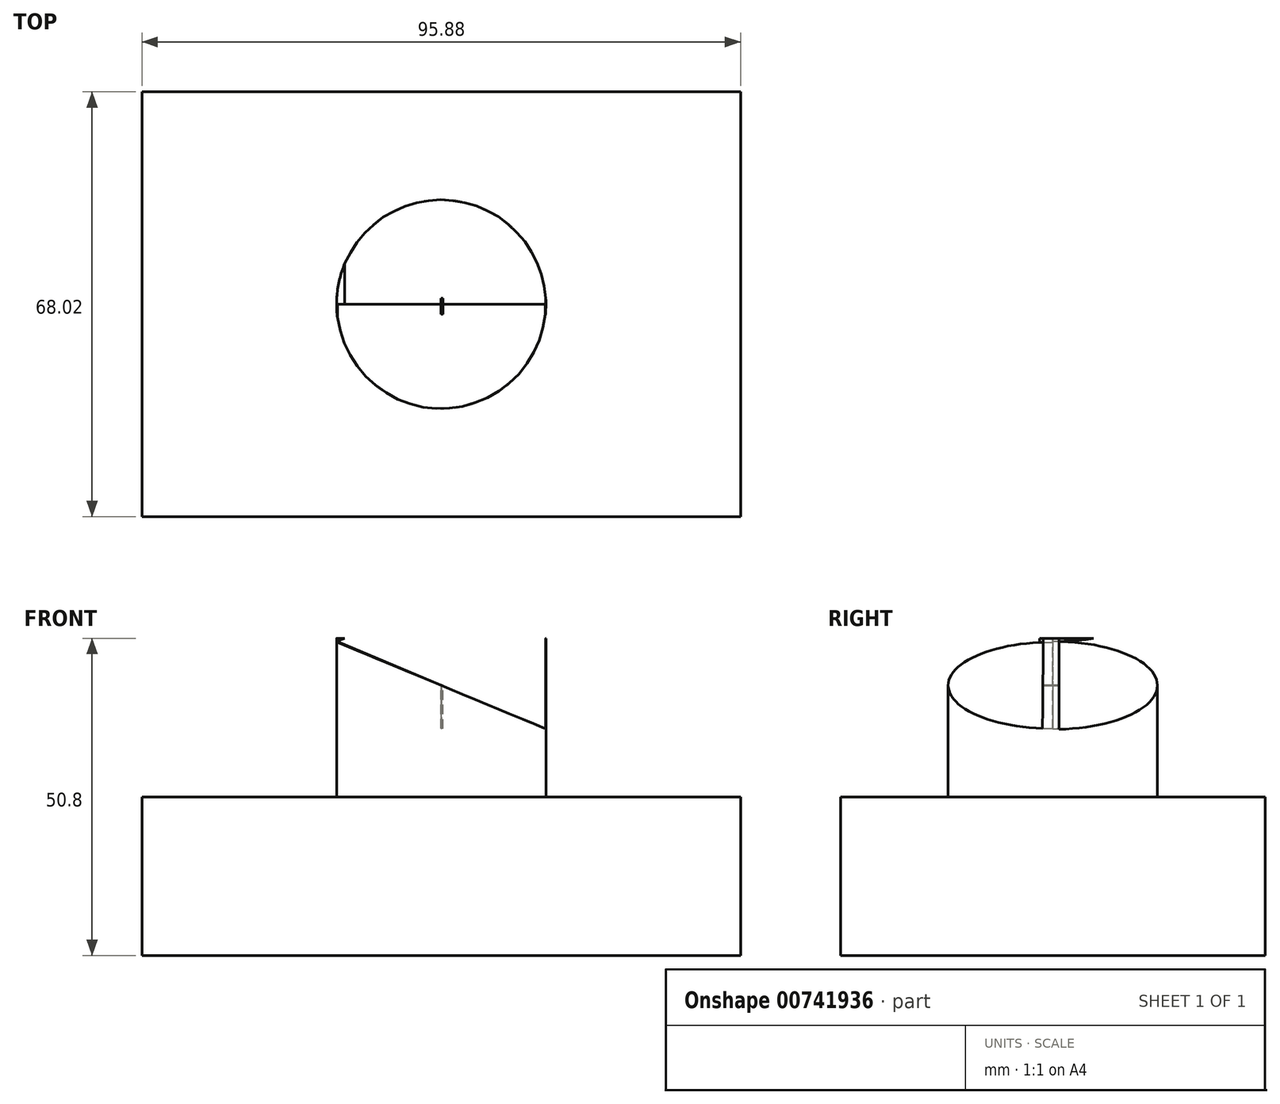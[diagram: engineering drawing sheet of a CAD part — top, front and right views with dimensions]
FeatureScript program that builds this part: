
annotation { "Feature Type Name" : "Feature", "Feature Type Description" : "" }
export const myFeature = defineFeature(function(context is Context, id is Id, definition is map)
    precondition{}
    {
        {
            var Q0;
            Q0=qCreatedBy(makeId("Top.planeOp"),FACE);
            var sketch = newSketch(context, id + "F0", { "sketchPlane" : qUnion([Q0])});
            skLineSegment(sketch, "E0.bottom", {"start": v(47.94, 34.01) * mm, "end": v(-47.94, 34.01) * mm});
            skLineSegment(sketch, "E0.top", {"start": v(47.94, -34.01) * mm, "end": v(-47.94, -34.01) * mm});
            skLineSegment(sketch, "E0.left", {"start": v(47.94, 34.01) * mm, "end": v(47.94, -34.01) * mm});
            skLineSegment(sketch, "E0.right", {"start": v(-47.94, 34.01) * mm, "end": v(-47.94, -34.01) * mm});
            skPoint(sketch, "E0.middle", {"position": v(0, 0) * mm});
            skCircle(sketch, "E1", {"center": v(0, 0) * mm, "radius": 16.77 * mm});
            skSolve(sketch);
        }
        {
            var Q0;
            Q0=makeQuery(id+"F0.imprint","IMPRINT",FACE,{"disambiguationData":[TD([[makeQuery(id+"F0.imprint","IMPRINT",EDGE,{"derivedFrom":sQuery(id+"F0.wireOp",EDGE,"E0.bottom")}),1.0]])]});
            extrude(context, id + "F1", {"entities" : qUnion([Q0]), "depth" : 25.4 * mm, "offsetDistance" : 25.4 * mm});
        }
        {
            var Q0;
            Q0=makeQuery(id+"F0.imprint","IMPRINT",FACE,{"disambiguationData":[TD([[makeQuery(id+"F0.imprint","IMPRINT",EDGE,{"derivedFrom":sQuery(id+"F0.wireOp",EDGE,"E1")}),1.0]])]});
            extrude(context, id + "F2", {"entities" : qUnion([Q0]), "operationType" : NewBodyOperationType.ADD, "depth" : 50.8 * mm, "offsetDistance" : 25.4 * mm});
        }
        {
            var Q0;
            Q0=qCreatedBy(makeId("Front.planeOp"),FACE);
            var sketch = newSketch(context, id + "F3", { "sketchPlane" : qUnion([Q0])});
            skLineSegment(sketch, "E2", {"start": v(-16.71, 50.3) * mm, "end": v(16.74, 36.21) * mm});
            skLineSegment(sketch, "E3", {"start": v(16.74, 36.21) * mm, "end": v(16.74, 50.9) * mm});
            skArc(sketch, "E4", {"start": v(16.74, 50.9) * mm, "mid": v(-0.04, 53.8) * mm, "end": v(-16.71, 50.3) * mm});
            skSolve(sketch);
        }
        {
            var Q0;
            Q0 = qSketchRegion(id + "F3", true);
            extrude(context, id + "F4", {"entities" : qUnion([Q0]), "operationType" : NewBodyOperationType.REMOVE, "oppositeDirection" : true, "depth" : 25.4 * mm, "offsetDistance" : 25.4 * mm});
        }
        {
            var Q0;
            Q0=qCreatedBy(makeId("Front.planeOp"),FACE);
            var sketch = newSketch(context, id + "F5", { "sketchPlane" : qUnion([Q0])});
            skLineSegment(sketch, "E5", {"start": v(16.69, 36.34) * mm, "end": v(-16.63, 50.15) * mm});
            skLineSegment(sketch, "E6", {"start": v(-16.63, 50.15) * mm, "end": v(16.69, 36.34) * mm});
            skLineSegment(sketch, "E7", {"start": v(16.7, 50.8) * mm, "end": v(16.69, 36.34) * mm});
            skLineSegment(sketch, "E8", {"start": v(16.7, 50.8) * mm, "end": v(-16.63, 50.83) * mm});
            skLineSegment(sketch, "E9", {"start": v(-16.63, 50.83) * mm, "end": v(-16.63, 50.15) * mm});
            skSolve(sketch);
        }
        {
            var Q0;
            Q0 = qSketchRegion(id + "F5", true);
            extrude(context, id + "F6", {"entities" : qUnion([Q0]), "operationType" : NewBodyOperationType.REMOVE, "depth" : 25.4 * mm, "offsetDistance" : 25.4 * mm});
        }
        {
            var Q0;
            Q0=qCreatedBy(makeId("Right.planeOp"),FACE);
            var sketch = newSketch(context, id + "F7", { "sketchPlane" : qUnion([Q0])});
            skLineSegment(sketch, "E10", {"start": v(-1.68, 36.35) * mm, "end": v(0.98, 36.35) * mm});
            skLineSegment(sketch, "E11", {"start": v(0.98, 36.35) * mm, "end": v(0.98, 50.87) * mm});
            skLineSegment(sketch, "E12", {"start": v(0.98, 50.87) * mm, "end": v(-1.46, 50.87) * mm});
            skLineSegment(sketch, "E13", {"start": v(-1.46, 50.87) * mm, "end": v(-1.68, 36.35) * mm});
            skSolve(sketch);
        }
        {
            var Q0;
            Q0 = qSketchRegion(id + "F7", true);
            extrude(context, id + "F8", {"entities" : qUnion([Q0]), "operationType" : NewBodyOperationType.REMOVE, "depth" : 0.25 * mm, "offsetDistance" : 25.4 * mm});
        }
        {
            var Q0;
            Q0=qCreatedBy(makeId("Right.planeOp"),FACE);
            var sketch = newSketch(context, id + "F9", { "sketchPlane" : qUnion([Q0])});
            skLineSegment(sketch, "E14", {"start": v(-1.65, 36.37) * mm, "end": v(0.97, 36.37) * mm});
            skLineSegment(sketch, "E15", {"start": v(0.97, 36.37) * mm, "end": v(0.97, 50.75) * mm});
            skLineSegment(sketch, "E16", {"start": v(0.97, 50.75) * mm, "end": v(-1.54, 50.75) * mm});
            skLineSegment(sketch, "E17", {"start": v(-1.54, 50.75) * mm, "end": v(-1.65, 36.37) * mm});
            skSolve(sketch);
        }
        {
            var Q0;
            Q0 = qSketchRegion(id + "F9", true);
            extrude(context, id + "F10", {"entities" : qUnion([Q0]), "operationType" : NewBodyOperationType.REMOVE, "depth" : -0.03 * mm, "offsetDistance" : 25.4 * mm});
        }
    });
